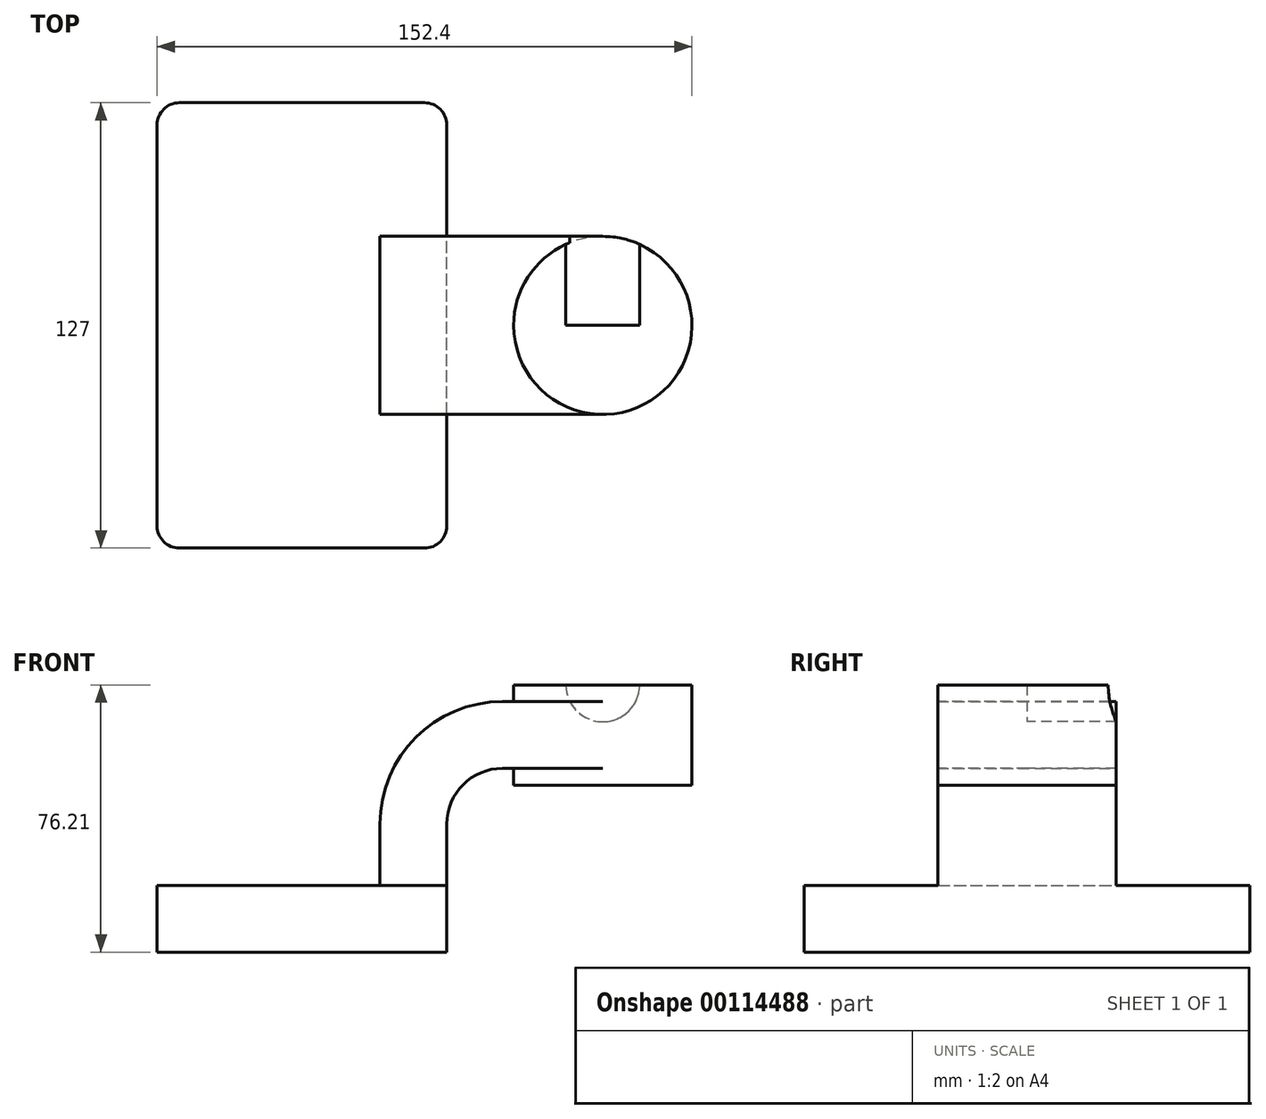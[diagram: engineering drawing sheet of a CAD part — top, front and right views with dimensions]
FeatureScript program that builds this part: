
annotation { "Feature Type Name" : "Feature", "Feature Type Description" : "" }
export const myFeature = defineFeature(function(context is Context, id is Id, definition is map)
    precondition{}
    {
        {
            var Q0;
            Q0=qCreatedBy(makeId("Front.planeOp"),FACE);
            var sketch = newSketch(context, id + "F0", { "sketchPlane" : qUnion([Q0])});
            skLineSegment(sketch, "E0.bottom", {"start": v(41.28, -9.52) * mm, "end": v(-41.28, -9.53) * mm});
            skLineSegment(sketch, "E0.top", {"start": v(41.28, 9.53) * mm, "end": v(-41.28, 9.52) * mm});
            skLineSegment(sketch, "E0.left", {"start": v(41.28, -9.52) * mm, "end": v(41.28, 9.53) * mm});
            skLineSegment(sketch, "E0.right", {"start": v(-41.28, -9.53) * mm, "end": v(-41.28, 9.52) * mm});
            skPoint(sketch, "E0.middle", {"position": v(0, 0) * mm});
            skLineSegment(sketch, "E1.bottom", {"start": v(111.12, 38.1) * mm, "end": v(60.32, 38.1) * mm});
            skLineSegment(sketch, "E1.top", {"start": v(111.12, 66.68) * mm, "end": v(60.32, 66.68) * mm});
            skLineSegment(sketch, "E1.left", {"start": v(111.12, 38.1) * mm, "end": v(111.12, 66.68) * mm});
            skLineSegment(sketch, "E1.right", {"start": v(60.32, 38.1) * mm, "end": v(60.32, 66.68) * mm});
            skPoint(sketch, "E1.middle", {"position": v(85.72, 52.39) * mm});
            skLineSegment(sketch, "E2", {"start": v(41.28, 9.53) * mm, "end": v(41.28, 27) * mm});
            skArc(sketch, "E3", {"start": v(41.28, 27) * mm, "mid": v(45.92, 38.23) * mm, "end": v(57.15, 42.88) * mm});
            skLineSegment(sketch, "E4", {"start": v(57.15, 42.88) * mm, "end": v(85.72, 42.88) * mm});
            skLineSegment(sketch, "E5.0", {"start": v(57.15, 61.93) * mm, "end": v(85.72, 61.93) * mm});
            skArc(sketch, "E5.1", {"start": v(22.23, 27) * mm, "mid": v(32.45, 51.7) * mm, "end": v(57.15, 61.93) * mm});
            skLineSegment(sketch, "E5.2", {"start": v(22.23, 9.53) * mm, "end": v(22.23, 27) * mm});
            skLineSegment(sketch, "E6", {"start": v(85.72, 38.1) * mm, "end": v(85.72, 66.68) * mm});
            skFitSpline(sketch, "E7", {"points": [v(-41.28, 9.53) * mm, v(57.15, 61.93) * mm], "startDerivative": vector(9.32, 61.7) * mm, "endDerivative": vector(128.5, -6.33) * mm});
            skSolve(sketch);
        }
        {
            var Q0;
            Q0=makeQuery(id+"F0.imprint","IMPRINT",FACE,{"disambiguationData":[TD([[makeQuery(id+"F0.imprint","IMPRINT",EDGE,{"derivedFrom":sQuery(id+"F0.wireOp",EDGE,"E0.bottom")}),-1.0]])]});
            extrude(context, id + "F1", {"entities" : qUnion([Q0]), "endBound" : BoundingType.SYMMETRIC, "depth" : 127 * mm});
        }
        {
            var Q0;
            {var subQ2=sQuery(id+"F0.wireOp",EDGE,"E2");Q0=makeQuery(id+"F0.imprint","IMPRINT",FACE,{"disambiguationData":[TD([[makeQuery(id+"F0.imprint","IMPRINT",EDGE,{"derivedFrom":subQ2}),1.0]])]});}
            var Q1;
            {var subQ0=sQuery(id+"F0.wireOp",EDGE,"E4");var subQ1=sQuery(id+"F0.wireOp",EDGE,"E1.right");var subQ2=makeQuery(id+"F0.imprint","INTERSECT",VERTEX,{"derivedFrom":[subQ1,subQ0]});Q1=makeQuery(id+"F0.imprint","IMPRINT",FACE,{"disambiguationData":[TD([[makeQuery(id+"F0.imprint","IMPRINT",EDGE,{"disambiguationData":[TD([[subQ2,-1.0]])],"derivedFrom":subQ1}),-1.0]])]});}
            extrude(context, id + "F2", {"entities" : qUnion([Q0, Q1]), "operationType" : NewBodyOperationType.ADD, "endBound" : BoundingType.SYMMETRIC, "depth" : 50.8 * mm});
        }
        {
            var Q0;
            Q0=makeQuery(id+"F0.imprint","IMPRINT",FACE,{"disambiguationData":[TD([[makeQuery(id+"F0.imprint","IMPRINT",EDGE,{"derivedFrom":sQuery(id+"F0.wireOp",EDGE,"E5.1")}),1.0]])]});
            extrude(context, id + "F3", {"entities" : qUnion([Q0]), "operationType" : NewBodyOperationType.ADD, "endBound" : BoundingType.SYMMETRIC, "depth" : 15.88 * mm});
        }
        {
            var Q0;
            {var subQ4=sQuery(id+"F0.wireOp",EDGE,"E1.left");Q0=makeQuery(id+"F0.imprint","IMPRINT",FACE,{"disambiguationData":[TD([[makeQuery(id+"F0.imprint","IMPRINT",EDGE,{"derivedFrom":subQ4}),1.0]])]});}
            var Q1;
            Q1=sQuery(id+"F0.wireOp",EDGE,"E6");
            revolve(context, id + "F4", {"operationType" : NewBodyOperationType.ADD, "entities" : qUnion([Q0]), "axis" : qUnion([Q1]), "revolveType" : RevolveType.FULL});
        }
        {
            var Q0;
            Q0=makeQuery(id+"F1.opExtrude","CAP_EDGE",EDGE,{"disambiguationData":[OSD([sQuery(id+"F0.wireOp",EDGE,"E0.right")])],"isStart":false});
            var Q1;
            Q1=makeQuery(id+"F1.opExtrude","CAP_EDGE",EDGE,{"disambiguationData":[OSD([sQuery(id+"F0.wireOp",EDGE,"E0.left")])],"isStart":false});
            var Q2;
            Q2=makeQuery(id+"F1.opExtrude","CAP_EDGE",EDGE,{"disambiguationData":[OSD([sQuery(id+"F0.wireOp",EDGE,"E0.left")])],"isStart":true});
            var Q3;
            Q3=makeQuery(id+"F1.opExtrude","CAP_EDGE",EDGE,{"disambiguationData":[OSD([sQuery(id+"F0.wireOp",EDGE,"E0.right")])],"isStart":true});
            fillet(context, id + "F5", {"entities" : qUnion([Q0, Q1, Q2, Q3]), "radius" : 6.35 * mm, "tangentPropagation" : true, "allowEdgeOverflow" : false});
        }
        {
            var Q0;
            Q0=sQuery(id+"F0.wireOp",VERTEX,"E6.end");
            var Q1;
            Q1=makeQuery(id+"F1.opExtrude","SWEPT_BODY",BODY,{"disambiguationData":[OSD([sQuery(id+"F0.wireOp",EDGE,"E0.bottom"),sQuery(id+"F0.wireOp",EDGE,"E0.top"),sQuery(id+"F0.wireOp",EDGE,"E0.left"),sQuery(id+"F0.wireOp",EDGE,"E0.right")])]});
            hole(context, id + "F6", {"style" : HoleStyle.SIMPLE, "endStyle" : HoleEndStyle.THROUGH, "standardTappedOrClearance" : lookupTablePath({ "standard" : "ANSI", "engagement" : "50%", "pitch" : "14 tpi", "size" : "7/8", "type" : "Tapped" }), "standardBlindInLast" : lookupTablePath({ "standard" : "ANSI", "engagement" : "50%", "pitch" : "14 tpi", "size" : "7/8", "type" : "Tapped" }), "holeDiameter" : 21.03 * mm, "locations" : qUnion([Q0]), "scope" : qUnion([Q1]), "isTappedThrough" : true, "majorDiameter" : 22.23 * mm, "showTappedDepth" : true});
        }
    });
